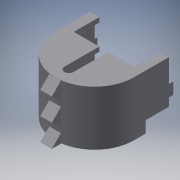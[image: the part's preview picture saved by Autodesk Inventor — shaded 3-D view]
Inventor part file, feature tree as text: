
AUTODESK INVENTOR PART (.ipt)
format: ipt  version: 2016 (Build 200138000, 138)  size: 286,720 bytes
history: native  units: in
note: dims shown in document units (in); Inventor stores cm internally (conversion verified against a paired STEP export)
features: sketch x15, extrude x14, reference x9, projected_geometry x2, plane x1
ambient origin geometry x8: Origin, YZ Plane, XZ Plane, XY Plane, X Axis, Y Axis, Z Axis, Center Point
bodies: Solid1 (feature_tree)
feature tree (41):
  extrude  "Extrusion1"  Depth=0.1969in TaperAngle=0.0deg
  extrude  "Extrusion2"  Depth=0.1969in TaperAngle=0.0deg
  extrude  "Extrusion3"  [1 undecoded]
  extrude  "Extrusion4"  Depth=0.3937in
  plane  "Work Plane1"
  sketch  "Sketch5"  dims[d12=1.9685in d14=0.9774in d15=0.3937in d17=1.0in d19=0.5in d20=0.0in]
  extrude  "Extrusion5"  Depth=1.0in TaperAngle=0.0deg
  extrude  "Extrusion6"  Depth=100.0in TaperAngle=0.0deg
  extrude  "Extrusion7"  Depth=56.0in TaperAngle=0.0deg
  extrude  "Extrusion8"  Depth=0.3937in
  extrude  "Extrusion9"  Depth=1.0in TaperAngle=0.0deg
  extrude  "Extrusion10"  Depth=0.0787in
  extrude  "Extrusion11"  Depth=0.0787in
  extrude  "Extrusion12"  Depth=0.1in TaperAngle=0.0deg
  extrude  "Extrusion13"  Depth=0.5in TaperAngle=0.0deg
  extrude  "Extrusion14"  [1 undecoded]
  sketch  "Sketch1"  dims[d0=0.1969in d1=1.5in d2=0.0in]
  reference  "Reference1"
  sketch  "Sketch2"  dims[d3=4.6969in d4=0.0in d5=0.1969in d6=0.0in]
  sketch  "Sketch3"  dims[d7=0.1969in d8=0.0in d9=-1.697in]
  sketch  "Sketch4"  dims[d10=0.7874in d11=0.3937in]
  reference  "Reference2"
  sketch  "Sketch6"  dims[d21=0.197in d22=0.0in d23=100.0in d24=0.0in]
  sketch  "Sketch8"  dims[d25=0.5in d26=56.0in d27=0.0in]
  reference  "Reference3"
  reference  "Reference4"
  reference  "Reference5"
  reference  "Reference6"
  sketch  "Sketch9"  dims[d28=0.3937in d29=0.3937in]
  sketch  "Sketch10"  dims[d30=56.0in d31=0.0in d32=1.0in d33=0.0in]
  sketch  "Sketch11"  dims[d34=0.0787in d35=0.0787in]
  sketch  "Sketch12"  dims[d36=0.0787in d37=0.0787in]
  sketch  "Sketch13"  dims[d38=1.0in d39=0.0in d40=0.1in d41=0.0in]
  reference  "Reference7"
  sketch  "Sketch14"  dims[d42=0.5in d43=0.0in d44=0.5in d45=0.0in]
  reference  "Reference8"
  reference  "Reference9"
  sketch  "Sketch15"
  projected_geometry  "Projected Loop1"
  projected_geometry  "Projected Loop2"
  sketch  "Sketch16"
note: 2 required parameter values undecoded (feature->parameter linkage not recoverable at this tier; creation-order binding heuristic only, values carry confidence <= 0.55)
